# Revit family: ALL2_63_UN_Downlighter_ETK
name_source: partatom
category: Lighting Fixtures
revit_build: Autodesk Revit 2017 (Build: 20190508_0315(x64)
units: mm (PartAtom-declared; Revit-internal decimal feet)

## family parameters
Always vertical = Yes
Cut with Voids When Loaded = No
Light Source = No
OmniClass Number = 23.80.70.11.14.11
OmniClass Title = Downlights
Part Type = Normal
Room Calculation Point = Yes
Round Connector Dimension = Use Diameter
Shared = No
Work Plane-Based = No

## types (16) — shared parameters
Assembly Code = 63.0
Bundle = 70°
Description = Downlighter
IfcExportAs = IfcLightFixtureType
IfcExportType = USERDEFINED
Lamp = LED
Luminaire_Body_Material = Aluminum 7175 T73 0 Hot Formed
Luminaire_Ring_Material = PPS Plastic
Manufacturer = ETK B.V.
Model = ALL.2
URL = https://www.etk.nl
Voltage = 230 V

## per-type parameters (varying)
| type | Apparent Load | Light Source | Wattage Comments |
| ALL.2100.15 - 19W / 2100lm / 3000K | 19 VA | ALL.2 - Lightsource : ALL.2100.15 - 19W / 2100lm / 3000k | 19W |
| ALL.2200.15 - 19W / 2200lm / 4000K | 19 VA | ALL.2 - Lightsource : ALL.2200.15 - 19W / 2200lm / 4000k | 19W |
| ALL.2300.15 - 24W / 2700lm / 3000K | 24 VA | ALL.2 - Lightsource : ALL.2300.15 - 24W / 2700lm / 3000k | 24W |
| ALL.2400.15 - 24W / 2800lm / 4000K | 24 VA | ALL.2 - Lightsource : ALL.2400.15 - 24W / 2800lm / 4000k | 24W |
| ALL.2103.15 - 19W / 2100lm / 3000K | 19 VA | ALL.2 - Lightsource : ALL.2103.15 - 19W / 2100lm / 3000k | 19W |
| ALL.2203.15 - 19W / 2200lm / 4000K | 19 VA | ALL.2 - Lightsource : ALL.2203.15 - 19W / 2200lm / 4000k | 19W |
| ALL.2303.15 - 24W / 2700lm / 3000K | 24 VA | ALL.2 - Lightsource : ALL.2303.15 - 24W / 2700lm / 3000k | 24W |
| ALL.2403.15 - 24W / 2800lm / 4000K | 24 VA | ALL.2 - Lightsource : ALL.2403.15 - 24W / 2800lm / 4000k | 24W |
| ALL.2110.15 - 19W / 2100lm / 3000K | 19 VA | ALL.2 - Lightsource : ALL.2110.15 - 19W / 2100lm / 3000k | 19W |
| ALL.2210.15 - 19W / 2200lm / 4000K | 19 VA | ALL.2 - Lightsource : ALL.2210.15 - 19W / 2200lm / 4000k | 19W |
| ALL.2310.15 - 24W / 2700lm / 3000K | 24 VA | ALL.2 - Lightsource : ALL.2310.15 - 24W / 2700lm / 3000k | 24W |
| ALL.2410.15 - 24W / 2800lm / 4000K | 24 VA | ALL.2 - Lightsource : ALL.2410.15 - 24W / 2800lm / 4000k | 24W |
| ALL.2113.15 - 19W / 2100lm / 3000K | 19 VA | ALL.2 - Lightsource : ALL.2113.15 - 19W / 2100lm / 3000k | 19W |
| ALL.2213.15 - 19W / 2200lm / 4000K | 19 VA | ALL.2 - Lightsource : ALL.2213.15 - 19W / 2200lm / 4000k | 19W |
| ALL.2313.15 - 24W / 2700lm / 3000K | 24 VA | ALL.2 - Lightsource : ALL.2313.15 - 24W / 2700lm / 3000k | 24W |
| ALL.2413.15 - 24W / 2800lm / 4000K | 24 VA | ALL.2 - Lightsource : ALL.2413.15 - 24W / 2800lm / 4000k | 24W |

## geometry (parser evidence)
native form markers: Sweep x5
no freeform markers — native parametric forms only
